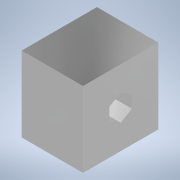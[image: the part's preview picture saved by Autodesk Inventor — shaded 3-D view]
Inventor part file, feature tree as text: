
AUTODESK INVENTOR PART (.ipt)
format: ipt  version: 2022.1 (Build 261234000, 234)  size: 88,064 bytes
history: native  units: mm (DEFAULTED — no unit token found)
features: other x8, extrude x2, sketch x2
bodies: Body1 (feature_tree)
feature tree (12):
  other  "Sólido1"
  other  "Origen"
  extrude  "Extrusión1"  Depth=7.5mm
  extrude  "Extrusión2"  Depth=10.0mm
  other  "Plano YZ"
  other  "Plano XZ"
  other  "Plano XY"
  other  "Eje X"
  other  "Eje Y"
  other  "Eje Z"
  sketch  "Boceto1"  dims[d0=3.4mm d2=7.5mm]
  sketch  "Boceto2"  dims[d3=15.0mm d4=0.0mm d5=3.175mm d6=10.0mm d7=0.0mm]
